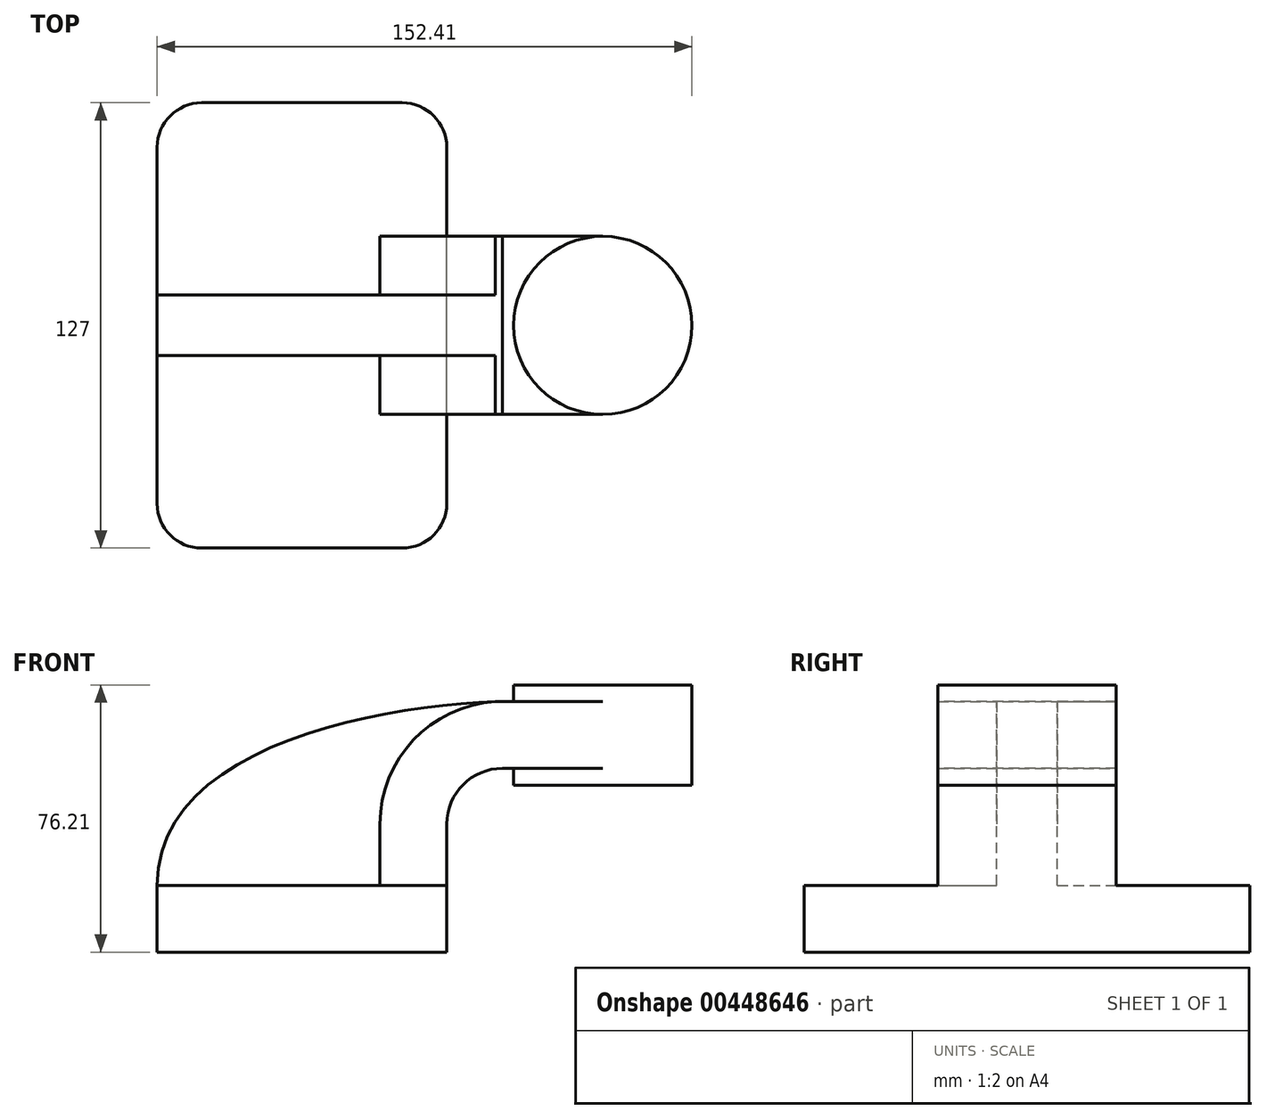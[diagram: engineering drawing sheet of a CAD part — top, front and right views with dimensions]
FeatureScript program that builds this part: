
annotation { "Feature Type Name" : "Feature", "Feature Type Description" : "" }
export const myFeature = defineFeature(function(context is Context, id is Id, definition is map)
    precondition{}
    {
        {
            var Q0;
            Q0=qCreatedBy(makeId("Front.planeOp"),FACE);
            var sketch = newSketch(context, id + "F0", { "sketchPlane" : qUnion([Q0])});
            skLineSegment(sketch, "E0.bottom", {"start": v(41.28, -9.52) * mm, "end": v(-41.28, -9.52) * mm});
            skLineSegment(sketch, "E0.top", {"start": v(41.27, 9.53) * mm, "end": v(-41.28, 9.53) * mm});
            skLineSegment(sketch, "E0.left", {"start": v(41.28, -9.52) * mm, "end": v(41.28, 9.53) * mm});
            skLineSegment(sketch, "E0.right", {"start": v(-41.28, -9.52) * mm, "end": v(-41.28, 9.53) * mm});
            skPoint(sketch, "E0.middle", {"position": v(0, 0) * mm});
            skLineSegment(sketch, "E1.bottom", {"start": v(111.12, 38.1) * mm, "end": v(60.32, 38.1) * mm});
            skLineSegment(sketch, "E1.top", {"start": v(111.12, 66.68) * mm, "end": v(60.32, 66.68) * mm});
            skLineSegment(sketch, "E1.left", {"start": v(111.13, 38.1) * mm, "end": v(111.13, 66.68) * mm});
            skLineSegment(sketch, "E1.right", {"start": v(60.32, 38.1) * mm, "end": v(60.32, 66.68) * mm});
            skLineSegment(sketch, "E2", {"start": v(41.27, 9.53) * mm, "end": v(41.27, 27) * mm});
            skArc(sketch, "E3", {"start": v(41.27, 27) * mm, "mid": v(45.92, 38.23) * mm, "end": v(57.15, 42.88) * mm});
            skLineSegment(sketch, "E4", {"start": v(57.15, 42.88) * mm, "end": v(85.72, 42.88) * mm});
            skLineSegment(sketch, "E5.0", {"start": v(57.15, 61.93) * mm, "end": v(85.72, 61.93) * mm});
            skArc(sketch, "E5.1", {"start": v(22.23, 27) * mm, "mid": v(32.45, 51.7) * mm, "end": v(57.15, 61.93) * mm});
            skLineSegment(sketch, "E5.2", {"start": v(22.22, 9.53) * mm, "end": v(22.22, 27) * mm});
            skLineSegment(sketch, "E6", {"start": v(85.72, 66.68) * mm, "end": v(85.72, 38.1) * mm});
            skFitSpline(sketch, "E7", {"points": [v(-41.28, 9.53) * mm, v(57.15, 61.93) * mm], "startDerivative": vector(-0.31, 119.48) * mm, "endDerivative": vector(104.45, 2.51) * mm});
            skSolve(sketch);
        }
        {
            var Q0;
            Q0=makeQuery(id+"F0.imprint","IMPRINT",FACE,{"disambiguationData":[TD([[makeQuery(id+"F0.imprint","IMPRINT",EDGE,{"derivedFrom":sQuery(id+"F0.wireOp",EDGE,"E0.bottom")}),-1.0]])]});
            extrude(context, id + "F1", {"entities" : qUnion([Q0]), "endBound" : BoundingType.SYMMETRIC, "depth" : 127 * mm});
        }
        {
            var Q0;
            {var subQ1=sQuery(id+"F0.wireOp",EDGE,"E2");Q0=makeQuery(id+"F0.imprint","IMPRINT",FACE,{"disambiguationData":[TD([[makeQuery(id+"F0.imprint","IMPRINT",EDGE,{"derivedFrom":subQ1}),1.0]])]});}
            var Q1;
            {var subQ0=sQuery(id+"F0.wireOp",EDGE,"E4");var subQ1=sQuery(id+"F0.wireOp",EDGE,"E1.right");var subQ2=makeQuery(id+"F0.imprint","INTERSECT",VERTEX,{"derivedFrom":[subQ1,subQ0]});Q1=makeQuery(id+"F0.imprint","IMPRINT",FACE,{"disambiguationData":[TD([[makeQuery(id+"F0.imprint","IMPRINT",EDGE,{"disambiguationData":[TD([[subQ2,-1.0]])],"derivedFrom":subQ1}),-1.0]])]});}
            extrude(context, id + "F2", {"entities" : qUnion([Q0, Q1]), "operationType" : NewBodyOperationType.ADD, "endBound" : BoundingType.SYMMETRIC, "depth" : 50.8 * mm});
        }
        {
            var Q0;
            {var subQ3=sQuery(id+"F0.wireOp",EDGE,"E5.2");Q0=makeQuery(id+"F0.imprint","IMPRINT",FACE,{"disambiguationData":[TD([[makeQuery(id+"F0.imprint","IMPRINT",EDGE,{"derivedFrom":subQ3}),1.0]])]});}
            extrude(context, id + "F3", {"entities" : qUnion([Q0]), "operationType" : NewBodyOperationType.ADD, "endBound" : BoundingType.SYMMETRIC, "depth" : 17.27 * mm});
        }
        {
            var Q0;
            {var subQ0=sQuery(id+"F0.wireOp",EDGE,"E1.left");Q0=makeQuery(id+"F0.imprint","IMPRINT",FACE,{"disambiguationData":[TD([[makeQuery(id+"F0.imprint","IMPRINT",EDGE,{"derivedFrom":subQ0}),1.0]])]});}
            var Q1;
            Q1=sQuery(id+"F0.wireOp",EDGE,"E6");
            revolve(context, id + "F4", {"operationType" : NewBodyOperationType.ADD, "entities" : qUnion([Q0]), "axis" : qUnion([Q1]), "revolveType" : RevolveType.FULL});
        }
        {
            var Q0;
            Q0=makeQuery(id+"F1.opExtrude","CAP_EDGE",EDGE,{"disambiguationData":[OSD([sQuery(id+"F0.wireOp",EDGE,"E0.left")])],"isStart":false});
            var Q1;
            Q1=makeQuery(id+"F1.opExtrude","CAP_EDGE",EDGE,{"disambiguationData":[OSD([sQuery(id+"F0.wireOp",EDGE,"E0.right")])],"isStart":false});
            var Q2;
            Q2=makeQuery(id+"F1.opExtrude","CAP_EDGE",EDGE,{"disambiguationData":[OSD([sQuery(id+"F0.wireOp",EDGE,"E0.left")])],"isStart":true});
            var Q3;
            Q3=makeQuery(id+"F1.opExtrude","CAP_EDGE",EDGE,{"disambiguationData":[OSD([sQuery(id+"F0.wireOp",EDGE,"E0.right")])],"isStart":true});
            fillet(context, id + "F5", {"entities" : qUnion([Q0, Q1, Q2, Q3]), "radius" : 12.7 * mm, "tangentPropagation" : true, "allowEdgeOverflow" : false});
        }
    });
